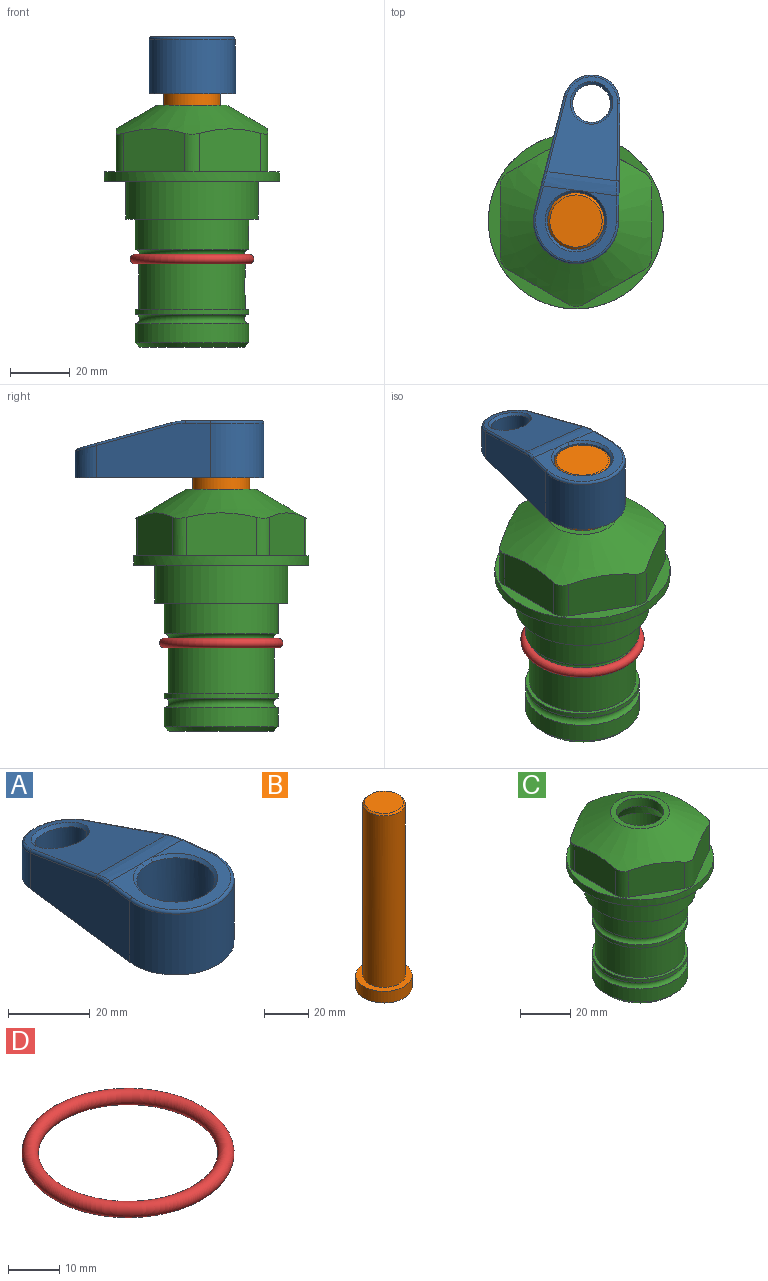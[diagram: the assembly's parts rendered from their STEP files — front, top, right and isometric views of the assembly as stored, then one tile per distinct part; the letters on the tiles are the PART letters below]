
ASSEMBLY  parts=4 mates=3
PART A: 31 faces, bbox 31.7x65.5x19.8 mm
  f0: plane 39.12x18.26mm, normal (0.99,0.12,0), area 612.2mm2, adj f1,f4,f7,f11,f13,f15
  f1: cylinder r=9.53mm len=18.91mm, axis (0,0,-1), area 296.1mm2, adj f0,f2,f7,f17
  f2: plane 39.12x18.26mm, normal (-0.99,0.12,0), area 612.2mm2, adj f1,f4,f7,f12,f14,f16
  f3: cylinder r=6.35mm len=12.7mm, axis (0,0,-1), area 362.4mm2, adj f7,f18
  f4: cylinder r=14.29mm len=28.58mm, axis (0,0,-1), area 882.2mm2, adj f0,f2,f7,f10
  f5: cylinder r=9.53mm len=19.05mm, axis (0,0,-1), area 1092.6mm2, adj f7,f19,f20
  f6: plane 26.99x23.69mm, normal (0,0,1), area 216.2mm2, adj f9,f10,f11,f12,f19
  f7: plane 63.5x28.58mm, normal (0,0,-1), area 661.8mm2, adj f0,f1,f2,f3,f4,f5,f22,f23
  f8: plane 33.52x23.6mm, normal (0,0.26,0.97), area 486mm2, adj f9,f15,f16,f17,f18
  f9: cylinder r=19.05mm len=24.72mm, axis (1,0,0), area 120.4mm2, adj f6,f8,f13,f14,f20
  f10: torus R=13.49mm, axis (0,0,1), area 59mm2, adj f4,f6,f11,f12
  f11: cylinder r=0.79mm len=8.67mm, axis (0.12,-0.99,0), area 10.8mm2, adj f0,f6,f10,f13
  f12: cylinder r=0.79mm len=8.67mm, axis (0.12,0.99,0), area 10.8mm2, adj f2,f6,f10,f14
  f13: bspline ~4.95x1.42mm, area 6.1mm2, adj f0,f9,f11,f15
  f14: bspline ~4.95x1.42mm, area 6.1mm2, adj f2,f9,f12,f16
  f15: cylinder r=0.79mm len=25.95mm, axis (0.12,-0.96,0.26), area 32.9mm2, adj f0,f8,f13,f17
  f16: cylinder r=0.79mm len=25.95mm, axis (0.12,0.96,-0.26), area 32.9mm2, adj f2,f8,f14,f17
  f17: bspline ~18.91x8.38mm, area 30mm2, adj f1,f8,f15,f16
  f18: bspline ~14.29x14.29mm, area 48.3mm2, adj f3,f8
  f19: cone r=9.53mm half-angle=45deg, axis (0,0,1), area 66.5mm2, adj f5,f6,f20
  f20: bspline ~3.22x0.96mm, area 3.5mm2, adj f5,f9,f19
  f21: plane 2.75x2.72mm, normal (0,0,-1), area 2.9mm2, adj f23,f25,f28
  f22: plane 23.05x15.88mm, normal (-0.99,-0.12,0), area 323.6mm2, adj f7,f25,f26,f27,f28,f29
  f23: plane 23.05x15.88mm, normal (0.99,-0.12,0), area 323.6mm2, adj f7,f21,f25,f27,f28,f30
  f24: cylinder r=9.53mm len=10.69mm, axis (0,0,-1), area 114.7mm2, adj f7,f27,f29,f30
  f25: cylinder r=12.7mm len=20.59mm, axis (0,0,-1), area 381.1mm2, adj f7,f21,f22,f23,f26,f28
  f26: plane 2.75x2.72mm, normal (0,0,-1), area 2.9mm2, adj f22,f25,f28
  f27: plane 19.72x18.37mm, normal (0,-0.26,-0.97), area 291.8mm2, adj f22,f23,f24,f28,f29,f30
  f28: cylinder r=15.88mm len=19.92mm, axis (1,0,0), area 54.8mm2, adj f21,f22,f23,f25,f26,f27
  f29: cylinder r=1.59mm len=11mm, axis (0,0,-1), area 34.7mm2, adj f7,f22,f24,f27
  f30: cylinder r=1.59mm len=11mm, axis (0,0,-1), area 34.7mm2, adj f7,f23,f24,f27
PART B: 6 faces, bbox 25.4x25.4x101.6 mm
  f0: plane 17.46x17.46mm, normal (0,0,1), area 239.5mm2, adj f5
  f1: plane 25.4x25.4mm, normal (0,0,-1), area 506.7mm2, adj f2
  f2: cylinder r=12.7mm len=25.4mm, axis (0,0,1), area 506.7mm2, adj f1,f3
  f3: plane 25.4x25.4mm, normal (0,0,1), area 221.7mm2, adj f2,f4
  f4: cylinder r=9.53mm len=94.46mm, axis (0,0,1), area 5653mm2, adj f3,f5
  f5: cone r=8.73mm half-angle=45deg, axis (0,0,-1), area 64.4mm2, adj f0,f4
PART C: 36 faces, bbox 58.7x58.7x81 mm
  f0: cylinder r=17.78mm len=35.56mm, axis (0,0,1), area 1670.8mm2, adj f23,f24,f31
  f1: cylinder r=19.05mm len=38.1mm, axis (0,0,1), area 1191.9mm2, adj f26,f27,f30
  f2: plane 58.66x58.66mm, normal (0,0,-1), area 1150.6mm2, adj f3,f28
  f3: cylinder r=29.33mm len=58.66mm, axis (0,0,-1), area 585.1mm2, adj f2,f4
  f4: plane 58.66x58.66mm, normal (0,0,1), area 475.9mm2, adj f3,f5,f6,f7,f8,f9,f10,f11
  f5: plane 20.32x14.34mm, normal (-0.5,0.87,0), area 324.4mm2, adj f4,f15,f16,f17
  f6: plane 20.32x14.34mm, normal (0.5,0.87,0), area 324.4mm2, adj f4,f14,f15,f17
  f7: plane 23.48x14.34mm, normal (1,0,0), area 324.4mm2, adj f4,f13,f14,f17
  f8: plane 20.32x14.34mm, normal (0.5,-0.87,0), area 324.4mm2, adj f4,f12,f13,f17
  f9: plane 20.32x14.34mm, normal (-0.5,-0.87,0), area 324.4mm2, adj f4,f11,f12,f17
  f10: plane 23.48x14.34mm, normal (-1,0,0), area 324.4mm2, adj f4,f11,f16,f17
  f11: cylinder r=5.08mm len=12.85mm, axis (0,0,-1), area 67.2mm2, adj f4,f9,f10,f17
  f12: cylinder r=5.08mm len=12.85mm, axis (0,0,-1), area 67.2mm2, adj f4,f8,f9,f17
  f13: cylinder r=5.08mm len=12.85mm, axis (0,0,-1), area 67.2mm2, adj f4,f7,f8,f17
  f14: cylinder r=5.08mm len=12.85mm, axis (0,0,-1), area 67.2mm2, adj f4,f6,f7,f17
  f15: cylinder r=5.08mm len=12.85mm, axis (0,0,-1), area 67.2mm2, adj f4,f5,f6,f17
  f16: cylinder r=5.08mm len=12.85mm, axis (0,0,-1), area 67.2mm2, adj f4,f5,f10,f17
  f17: cone r=11.73mm half-angle=60deg, axis (0,0,-1), area 2071.8mm2, adj f5,f6,f7,f8,f9,f10,f11,f12
  f18: plane 23.46x23.46mm, normal (0,0,1), area 147.4mm2, adj f17,f35
  f19: plane 34.93x34.93mm, normal (0,0,-1), area 958mm2, adj f29
  f20: cylinder r=19.05mm len=38.1mm, axis (0,0,1), area 760.1mm2, adj f21,f29
  f21: torus R=19.05mm, axis (0,0,1), area 565.3mm2, adj f20,f22
  f22: cylinder r=19.05mm len=38.1mm, axis (0,0,1), area 190mm2, adj f21,f23
  f23: plane 38.1x38.1mm, normal (0,0,1), area 146.9mm2, adj f0,f22
  f24: plane 38.1x38.1mm, normal (0,0,-1), area 146.9mm2, adj f0,f25
  f25: cylinder r=19.05mm len=38.1mm, axis (0,0,1), area 190mm2, adj f24,f26
  f26: torus R=19.05mm, axis (0,0,1), area 565.3mm2, adj f1,f25
  f27: plane 44.45x44.45mm, normal (0,0,-1), area 411.7mm2, adj f1,f28
  f28: cylinder r=22.23mm len=44.45mm, axis (0,0,1), area 1773.5mm2, adj f2,f27
  f29: cone r=19.05mm half-angle=45deg, axis (0,0,1), area 257.5mm2, adj f19,f20
  f30: cylinder r=3.17mm len=6.75mm, axis (-1,0,0), area 128mm2, adj f1,f33
  f31: cylinder r=3.17mm len=6.35mm, axis (-1,0,0), area 102.5mm2, adj f0,f33
  f32: plane 25.4x25.4mm, normal (0,0,1), area 506.7mm2, adj f33
  f33: cylinder r=12.7mm len=66.42mm, axis (0,0,-1), area 5236.2mm2, adj f30,f31,f32,f34
  f34: cone r=9.53mm half-angle=30deg, axis (0,0,-1), area 443.4mm2, adj f33,f35
  f35: cylinder r=9.53mm len=19.05mm, axis (0,0,-1), area 240.9mm2, adj f18,f34
PART D: 1 faces, bbox 44.7x44.7x3.2 mm
  f0: torus R=19.05mm, axis (0,0,1), area 1193.9mm2
PLACE A rot(axis=(0,0,-1),7.5deg) t=(0,0,-15.14)mm
PLACE B rot(axis=(0,0,-1),7.5deg) t=(0,0,-15.94)mm
PLACE C at identity fixed
PLACE D t=(0,0,-1.59)mm
MATE fastened D.f0 <-> C.f0  axis (0,0,1) through (0,0,-26.1)mm
MATE fastened A.f4 <-> B.f2  axis (0,0,-1) through (0,0,47.56)mm
MATE cylindrical B.f2 <-> C.f0  axis (0,0,1) through (0,0,-47.69)mm
